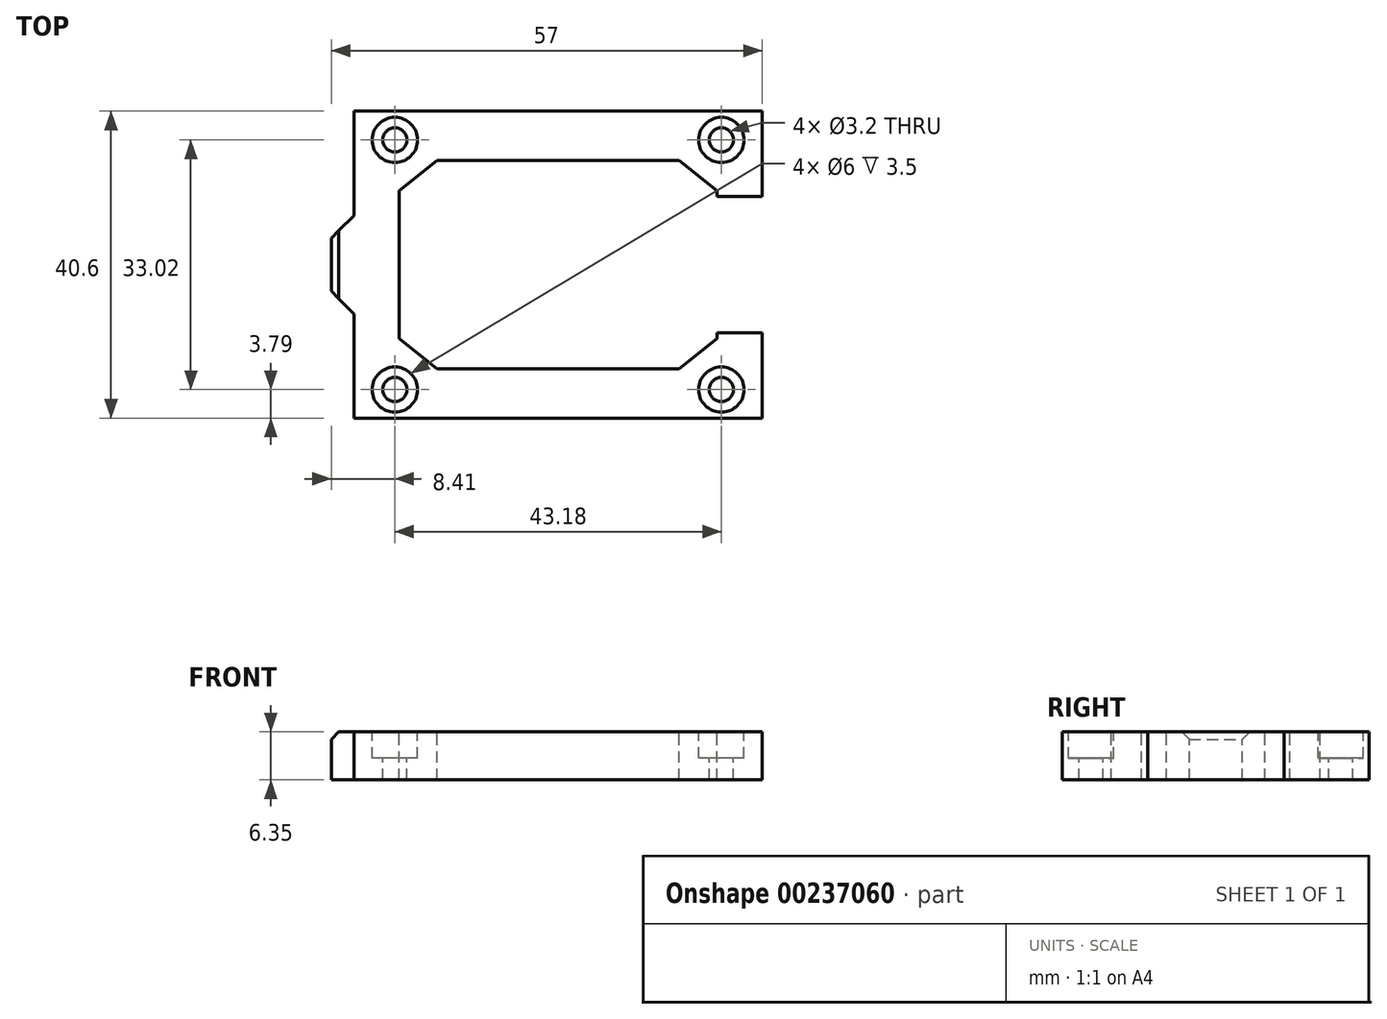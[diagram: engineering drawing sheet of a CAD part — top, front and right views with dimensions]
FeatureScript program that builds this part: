
annotation { "Feature Type Name" : "Feature", "Feature Type Description" : "" }
export const myFeature = defineFeature(function(context is Context, id is Id, definition is map)
    precondition{}
    {
        {
            var Q0;
            Q0=qCreatedBy(makeId("Top.planeOp"),FACE);
            var sketch = newSketch(context, id + "F0", { "sketchPlane" : qUnion([Q0])});
            skLineSegment(sketch, "E0.bottom", {"start": v(21.59, -16.5) * mm, "end": v(-21.59, -16.51) * mm, "construction": true});
            skLineSegment(sketch, "E0.top", {"start": v(21.59, 16.51) * mm, "end": v(-21.59, 16.5) * mm, "construction": true});
            skLineSegment(sketch, "E0.left", {"start": v(21.59, -16.5) * mm, "end": v(21.59, 16.51) * mm, "construction": true});
            skLineSegment(sketch, "E0.right", {"start": v(-21.59, -16.51) * mm, "end": v(-21.59, 16.5) * mm, "construction": true});
            skPoint(sketch, "E0.middle", {"position": v(0, 0) * mm});
            skLineSegment(sketch, "E1.bottom", {"start": v(27, -20.3) * mm, "end": v(-27, -20.3) * mm});
            skLineSegment(sketch, "E1.top", {"start": v(27, 20.3) * mm, "end": v(-27, 20.3) * mm});
            skLineSegment(sketch, "E1.left", {"start": v(27, -20.3) * mm, "end": v(27, -9) * mm});
            skLineSegment(sketch, "E1.right", {"start": v(-27, -20.3) * mm, "end": v(-27, -6.5) * mm});
            skLineSegment(sketch, "E2.0", {"start": v(16, 13.8) * mm, "end": v(-16, 13.8) * mm});
            skLineSegment(sketch, "E3", {"start": v(-27, 6.5) * mm, "end": v(-30, 3.5) * mm});
            skLineSegment(sketch, "E4", {"start": v(-30, 3.5) * mm, "end": v(-30, -3.5) * mm});
            skLineSegment(sketch, "E5", {"start": v(-30, -3.5) * mm, "end": v(-27, -6.5) * mm});
            skLineSegment(sketch, "E6.0", {"start": v(-21, -9.8) * mm, "end": v(-21, 9.8) * mm});
            skLineSegment(sketch, "E7.trimOffspring", {"start": v(-27, 6.5) * mm, "end": v(-27, 20.3) * mm});
            skLineSegment(sketch, "E8.0", {"start": v(21, -9.8) * mm, "end": v(21, -9) * mm});
            skLineSegment(sketch, "E9.trimOffspring", {"start": v(16, -13.8) * mm, "end": v(-16, -13.8) * mm});
            skLineSegment(sketch, "E10.bottom", {"start": v(27, -9) * mm, "end": v(21, -9) * mm});
            skLineSegment(sketch, "E10.top", {"start": v(27, 9) * mm, "end": v(21, 9) * mm});
            skLineSegment(sketch, "E11.trimOffspring", {"start": v(21, 9) * mm, "end": v(21, 9.8) * mm});
            skLineSegment(sketch, "E12.trimOffspring", {"start": v(27, 9) * mm, "end": v(27, 20.3) * mm});
            skLineSegment(sketch, "E13", {"start": v(-21, 9.8) * mm, "end": v(-16, 13.8) * mm});
            skPoint(sketch, "E14.orphan", {"position": v(-21, 13.8) * mm});
            skLineSegment(sketch, "E15.MirrorCS", {"start": v(-21, -9.8) * mm, "end": v(-16, -13.8) * mm});
            skLineSegment(sketch, "E16.MirrorCS", {"start": v(21, -9.8) * mm, "end": v(16, -13.8) * mm});
            skLineSegment(sketch, "E17.MirrorCS", {"start": v(21, 9.8) * mm, "end": v(16, 13.8) * mm});
            skPoint(sketch, "E18.orphan", {"position": v(-21, -13.8) * mm});
            skSolve(sketch);
        }
        {
            var Q0;
            Q0=qSketchRegion(id+"F0",true);
            extrude(context, id + "F1", {"entities" : qUnion([Q0]), "oppositeDirection" : true, "depth" : 6.35 * mm});
        }
        {
            var Q0;
            Q0=sQuery(id+"F0.wireOp",VERTEX,"E0.right.start");
            var Q1;
            Q1=sQuery(id+"F0.wireOp",VERTEX,"E0.bottom.start");
            var Q2;
            Q2=sQuery(id+"F0.wireOp",VERTEX,"E0.left.end");
            var Q3;
            Q3=sQuery(id+"F0.wireOp",VERTEX,"E0.right.end");
            var Q4;
            Q4=makeQuery(id+"F1.opExtrude","SWEPT_BODY",BODY,{"disambiguationData":[OSD([sQuery(id+"F0.wireOp",EDGE,"E1.bottom"),sQuery(id+"F0.wireOp",EDGE,"E1.top"),sQuery(id+"F0.wireOp",EDGE,"E1.left"),sQuery(id+"F0.wireOp",EDGE,"E1.right"),sQuery(id+"F0.wireOp",EDGE,"E2.0"),sQuery(id+"F0.wireOp",EDGE,"E3"),sQuery(id+"F0.wireOp",EDGE,"E4"),sQuery(id+"F0.wireOp",EDGE,"E5"),sQuery(id+"F0.wireOp",EDGE,"E6.0"),sQuery(id+"F0.wireOp",EDGE,"E7.trimOffspring"),sQuery(id+"F0.wireOp",EDGE,"E8.0"),sQuery(id+"F0.wireOp",EDGE,"E9.trimOffspring"),sQuery(id+"F0.wireOp",EDGE,"E10.bottom"),sQuery(id+"F0.wireOp",EDGE,"E10.top"),sQuery(id+"F0.wireOp",EDGE,"E11.trimOffspring"),sQuery(id+"F0.wireOp",EDGE,"E12.trimOffspring"),sQuery(id+"F0.wireOp",EDGE,"E13"),sQuery(id+"F0.wireOp",EDGE,"E15.MirrorCS"),sQuery(id+"F0.wireOp",EDGE,"E16.MirrorCS"),sQuery(id+"F0.wireOp",EDGE,"E17.MirrorCS")])]});
            hole(context, id + "F2", {"style" : HoleStyle.C_BORE, "endStyle" : HoleEndStyle.THROUGH, "holeDiameter" : 3.2 * mm, "cBoreDiameter" : 6 * mm, "cBoreDepth" : 3.5 * mm, "locations" : qUnion([Q0, Q1, Q2, Q3]), "scope" : qUnion([Q4]), "isTappedThrough" : true});
        }
        {
            var Q0;
            Q0=makeQuery(id+"F1.opExtrude","CAP_EDGE",EDGE,{"disambiguationData":[OSD([sQuery(id+"F0.wireOp",EDGE,"E4")])],"isStart":true});
            chamfer(context, id + "F3", {"entities" : qUnion([Q0]), "width" : 1 * mm, "tangentPropagation" : true});
        }
    });
